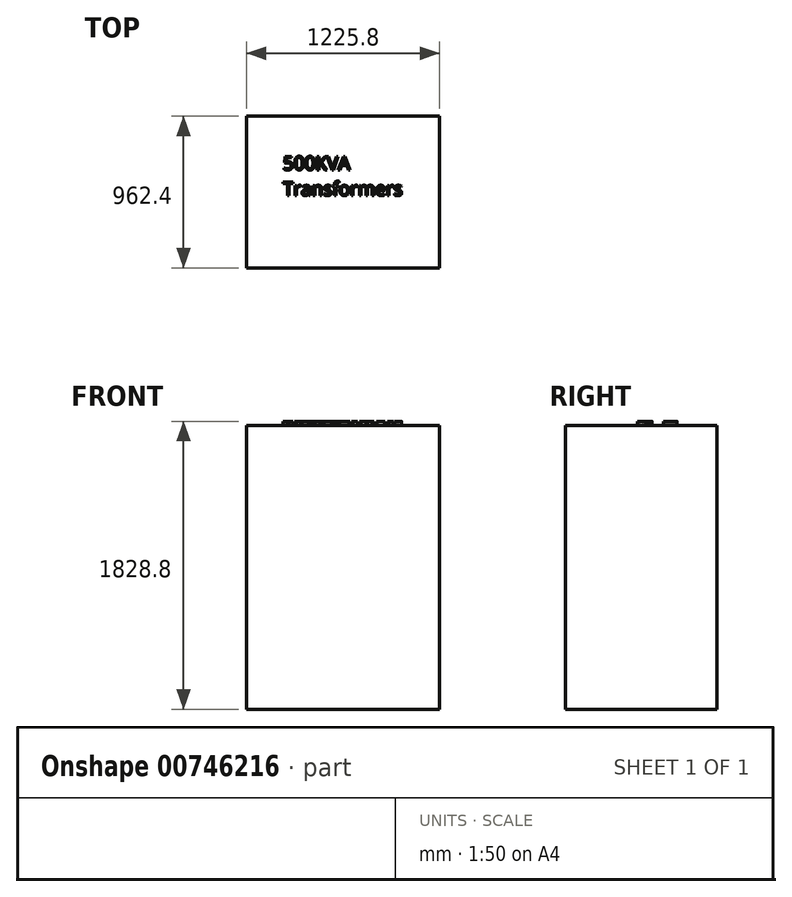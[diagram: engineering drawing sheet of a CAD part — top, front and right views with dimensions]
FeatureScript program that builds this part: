
annotation { "Feature Type Name" : "Feature", "Feature Type Description" : "" }
export const myFeature = defineFeature(function(context is Context, id is Id, definition is map)
    precondition{}
    {
        {
            var Q0;
            Q0=qCreatedBy(makeId("Top.planeOp"),FACE);
            var sketch = newSketch(context, id + "F0", { "sketchPlane" : qUnion([Q0])});
            skLineSegment(sketch, "E0.bottom", {"start": v(612.9, -481.2) * mm, "end": v(-612.9, -481.2) * mm});
            skLineSegment(sketch, "E0.top", {"start": v(612.9, 481.2) * mm, "end": v(-612.9, 481.2) * mm});
            skLineSegment(sketch, "E0.left", {"start": v(612.9, -481.2) * mm, "end": v(612.9, 481.2) * mm});
            skLineSegment(sketch, "E0.right", {"start": v(-612.9, -481.2) * mm, "end": v(-612.9, 481.2) * mm});
            skPoint(sketch, "E0.middle", {"position": v(0, 0) * mm});
            skSolve(sketch);
        }
        {
            var Q0;
            Q0 = qSketchRegion(id + "F0", true);
            extrude(context, id + "F1", {"entities" : qUnion([Q0]), "depth" : 1803.4 * mm, "offsetDistance" : 25.4 * mm});
        }
        {
            var Q0;
            Q0=makeQuery(id+"F1.opExtrude","CAP_FACE",FACE,{"disambiguationData":[OSD([sQuery(id+"F0.wireOp",EDGE,"E0.bottom"),sQuery(id+"F0.wireOp",EDGE,"E0.top"),sQuery(id+"F0.wireOp",EDGE,"E0.left"),sQuery(id+"F0.wireOp",EDGE,"E0.right")])],"isStart":false});
            var sketch = newSketch(context, id + "F2", { "sketchPlane" : qUnion([Q0])});
            skText(sketch, "E1", { "text": "500KVA \nTransformers", "fontName": "OpenSans-Regular.ttf"});
            const initialGuessF2  = {"E1": [-0.381, 0.14087, 1, 0, 0.08633]};
            skSetInitialGuess(sketch, initialGuessF2);
            skSolve(sketch);
        }
        {
            var Q0;
            Q0 = qSketchRegion(id + "F2", true);
            extrude(context, id + "F3", {"entities" : qUnion([Q0]), "operationType" : NewBodyOperationType.ADD, "depth" : 25.4 * mm, "offsetDistance" : 25.4 * mm});
        }
    });
